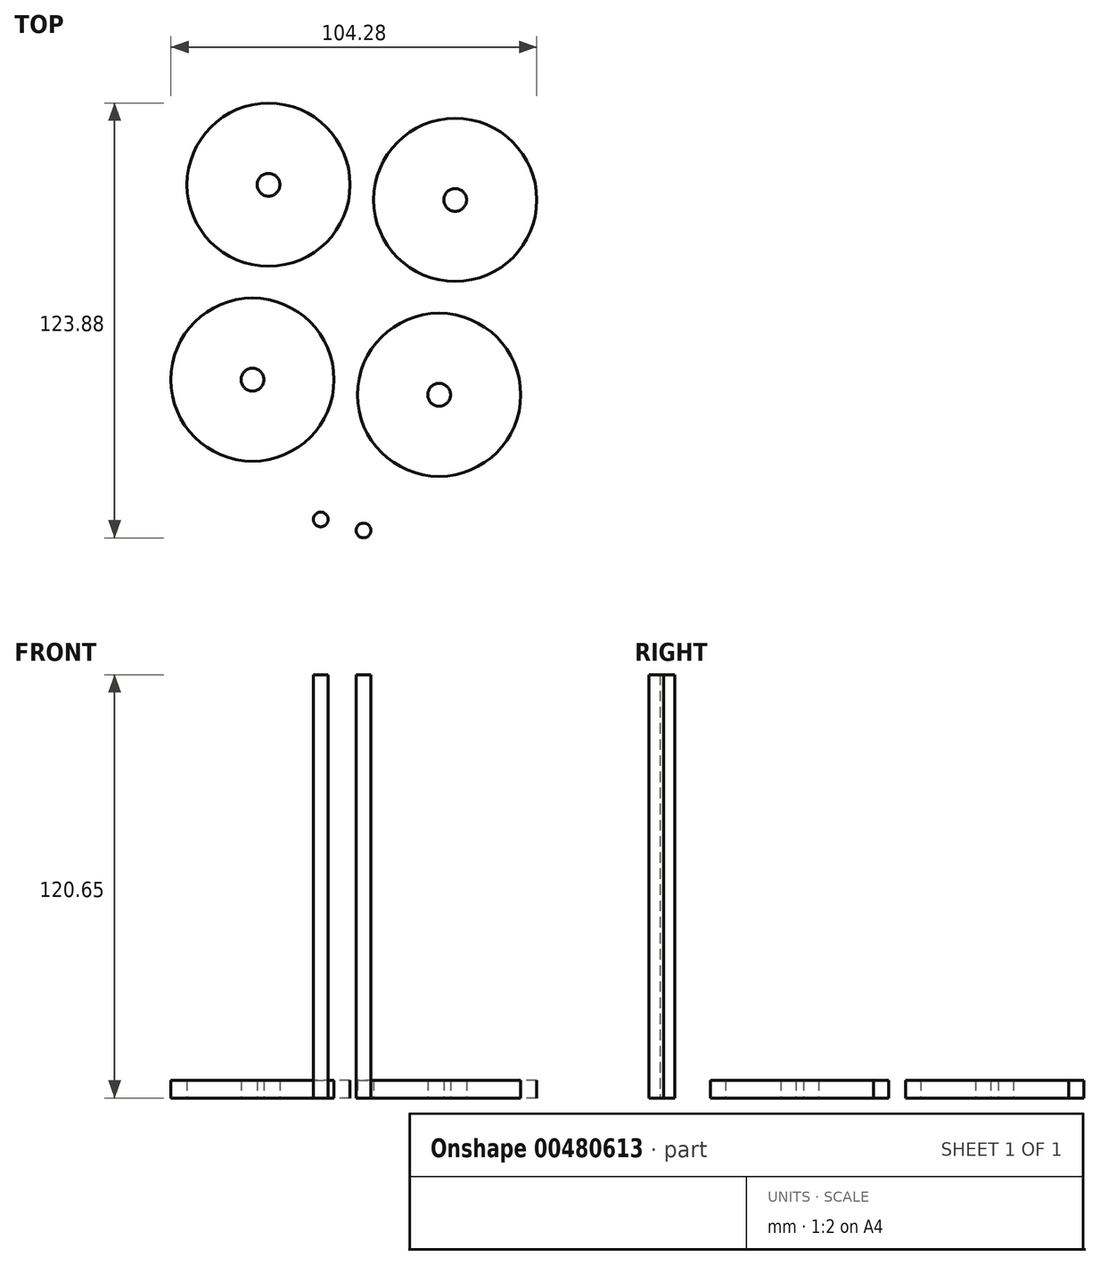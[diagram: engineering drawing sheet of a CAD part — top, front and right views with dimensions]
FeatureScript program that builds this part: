
annotation { "Feature Type Name" : "Feature", "Feature Type Description" : "" }
export const myFeature = defineFeature(function(context is Context, id is Id, definition is map)
    precondition{}
    {
        {
            var Q0;
            Q0=qCreatedBy(makeId("Top.planeOp"),FACE);
            var sketch = newSketch(context, id + "F0", { "sketchPlane" : qUnion([Q0])});
            skCircle(sketch, "E0", {"center": v(-40.58, 37.41) * mm, "radius": 3.25 * mm});
            skCircle(sketch, "E1", {"center": v(-40.58, 37.41) * mm, "radius": 23.25 * mm});
            skCircle(sketch, "E2", {"center": v(12.62, 33.1) * mm, "radius": 3.25 * mm});
            skCircle(sketch, "E3", {"center": v(12.62, 33.1) * mm, "radius": 23.25 * mm});
            skCircle(sketch, "E4", {"center": v(-45.16, -18.13) * mm, "radius": 3.25 * mm});
            skCircle(sketch, "E5", {"center": v(-45.16, -18.13) * mm, "radius": 23.25 * mm});
            skCircle(sketch, "E6", {"center": v(8.04, -22.45) * mm, "radius": 3.25 * mm});
            skCircle(sketch, "E7", {"center": v(8.04, -22.45) * mm, "radius": 23.25 * mm});
            skSolve(sketch);
        }
        {
            var Q0;
            Q0 = qSketchRegion(id + "F0", true);
            extrude(context, id + "F1", {"entities" : qUnion([Q0]), "depth" : 5.08 * mm, "offsetDistance" : 25.4 * mm});
        }
        {
            var Q0;
            Q0=qCreatedBy(makeId("Top.planeOp"),FACE);
            var sketch = newSketch(context, id + "F2", { "sketchPlane" : qUnion([Q0])});
            skCircle(sketch, "E8", {"center": v(-25.7, -57.98) * mm, "radius": 2.1 * mm});
            skCircle(sketch, "E9", {"center": v(-13.49, -61.12) * mm, "radius": 2.1 * mm});
            skSolve(sketch);
        }
        {
            var Q0;
            Q0 = qSketchRegion(id + "F2", true);
            extrude(context, id + "F3", {"entities" : qUnion([Q0]), "depth" : 120.65 * mm, "offsetDistance" : 25.4 * mm});
        }
    });
